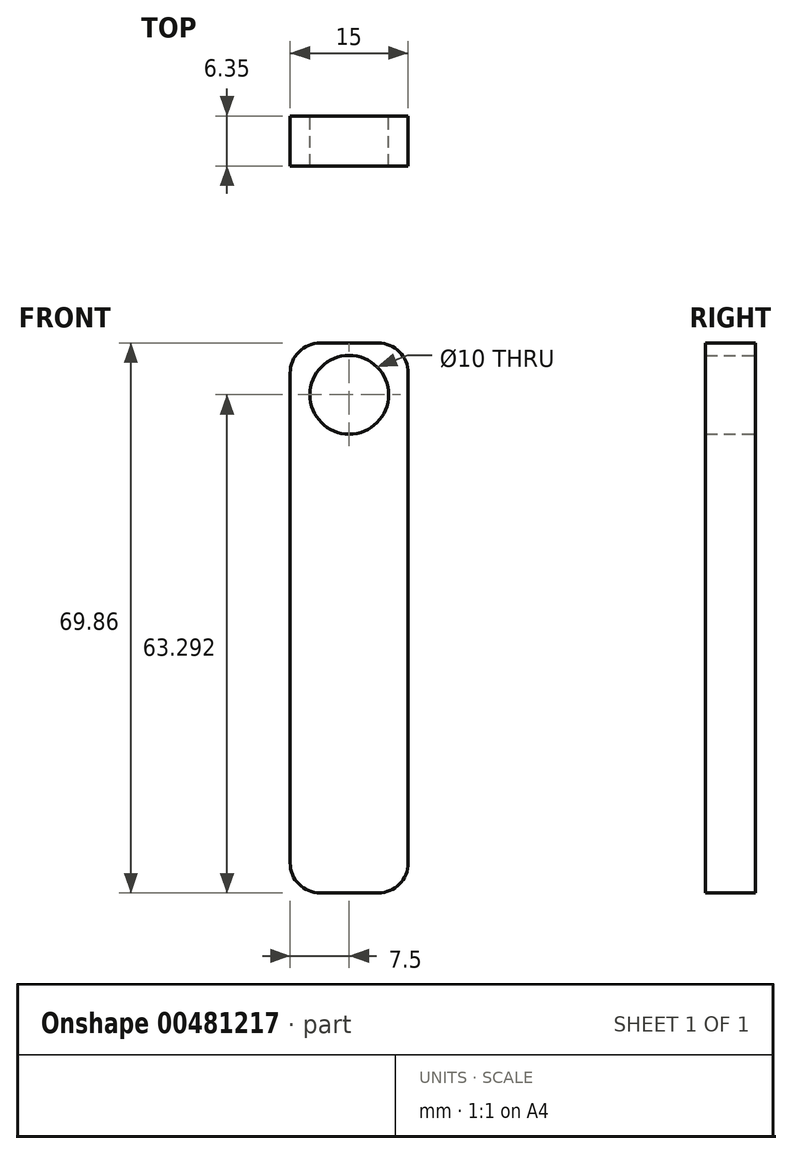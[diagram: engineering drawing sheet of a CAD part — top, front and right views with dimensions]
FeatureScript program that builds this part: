
annotation { "Feature Type Name" : "Feature", "Feature Type Description" : "" }
export const myFeature = defineFeature(function(context is Context, id is Id, definition is map)
    precondition{}
    {
        {
            var Q0;
            Q0=qCreatedBy(makeId("Front.planeOp"),FACE);
            var sketch = newSketch(context, id + "F0", { "sketchPlane" : qUnion([Q0])});
            skLineSegment(sketch, "E0.bottom", {"start": v(-3.69, 34.92) * mm, "end": v(3.7, 34.92) * mm});
            skLineSegment(sketch, "E0.top", {"start": v(-3.7, -34.93) * mm, "end": v(3.69, -34.93) * mm});
            skLineSegment(sketch, "E0.left", {"start": v(-7.5, 31.11) * mm, "end": v(-7.5, -31.12) * mm});
            skLineSegment(sketch, "E0.right", {"start": v(7.5, 31.11) * mm, "end": v(7.5, -31.12) * mm});
            skPoint(sketch, "E0.middle", {"position": v(0, 0) * mm});
            skCircle(sketch, "E1", {"center": v(0, 28.36) * mm, "radius": 5 * mm});
            skPoint(sketch, "E2.visualSharp", {"position": v(-7.5, 34.92) * mm});
            skArc(sketch, "E2.filletArc", {"start": v(-3.69, 34.92) * mm, "mid": v(-6.38, 33.8) * mm, "end": v(-7.5, 31.11) * mm});
            skPoint(sketch, "E3.visualSharp", {"position": v(7.5, 34.92) * mm});
            skArc(sketch, "E3.filletArc", {"start": v(7.5, 31.11) * mm, "mid": v(6.38, 33.8) * mm, "end": v(3.7, 34.92) * mm});
            skPoint(sketch, "E4.visualSharp", {"position": v(-7.5, -34.93) * mm});
            skArc(sketch, "E4.filletArc", {"start": v(-7.5, -31.12) * mm, "mid": v(-6.38, -33.8) * mm, "end": v(-3.7, -34.93) * mm});
            skPoint(sketch, "E5.visualSharp", {"position": v(7.5, -34.93) * mm});
            skArc(sketch, "E5.filletArc", {"start": v(3.69, -34.93) * mm, "mid": v(6.38, -33.8) * mm, "end": v(7.5, -31.12) * mm});
            skSolve(sketch);
        }
        {
            var Q0;
            Q0=makeQuery(id+"F0.imprint","IMPRINT",FACE,{"disambiguationData":[TD([[makeQuery(id+"F0.imprint","IMPRINT",EDGE,{"derivedFrom":sQuery(id+"F0.wireOp",EDGE,"E0.bottom")}),-1.0]])]});
            extrude(context, id + "F1", {"entities" : qUnion([Q0]), "depth" : 6.35 * mm});
        }
    });
